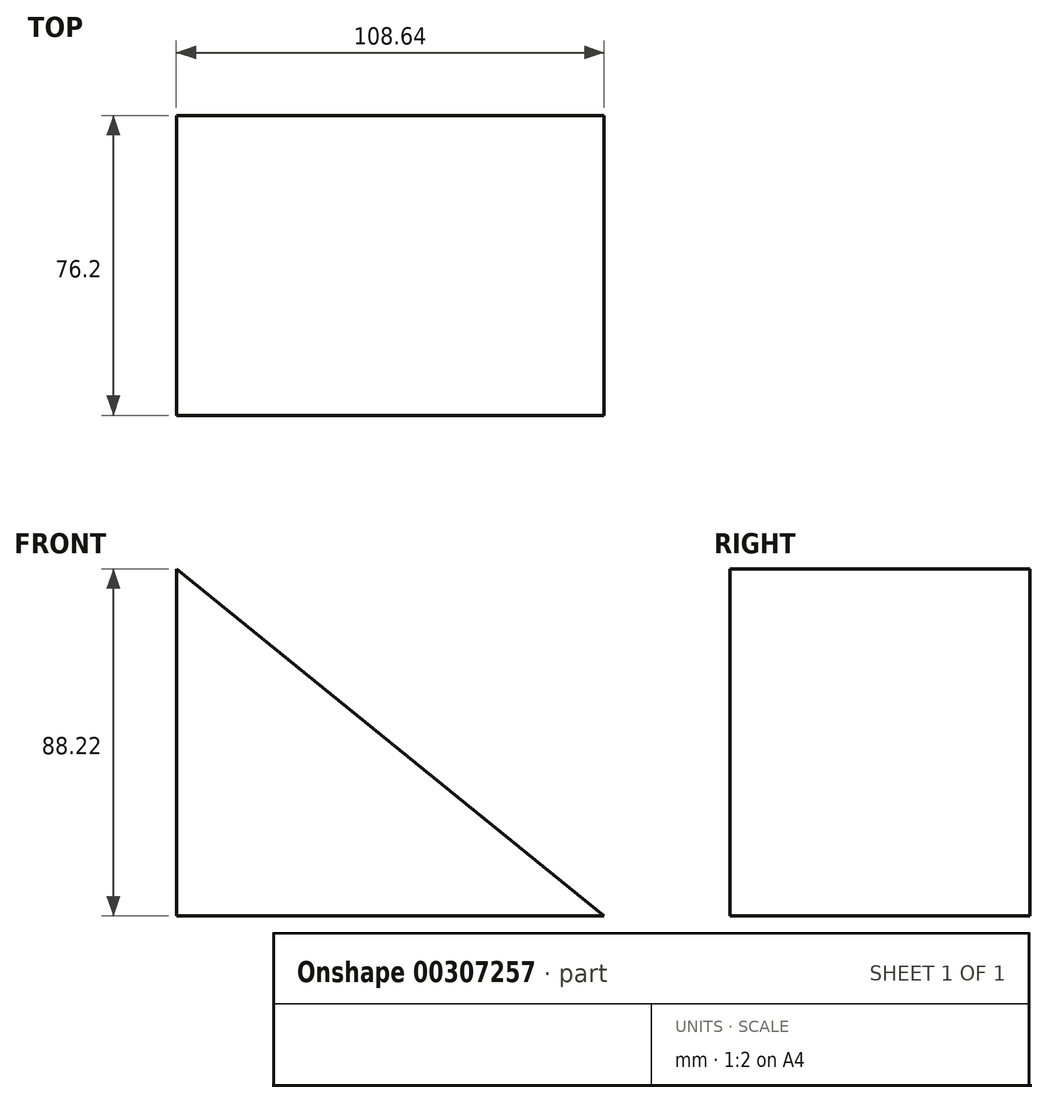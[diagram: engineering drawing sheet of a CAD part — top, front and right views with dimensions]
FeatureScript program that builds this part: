
annotation { "Feature Type Name" : "Feature", "Feature Type Description" : "" }
export const myFeature = defineFeature(function(context is Context, id is Id, definition is map)
    precondition{}
    {
        {
            var Q0;
            Q0=qCreatedBy(makeId("Front.planeOp"),FACE);
            var sketch = newSketch(context, id + "F0", { "sketchPlane" : qUnion([Q0])});
            skLineSegment(sketch, "E0", {"start": v(-51.69, -43.49) * mm, "end": v(56.95, -43.49) * mm});
            skLineSegment(sketch, "E1", {"start": v(56.95, -43.49) * mm, "end": v(-51.69, 44.73) * mm});
            skLineSegment(sketch, "E2", {"start": v(-51.69, 44.73) * mm, "end": v(-51.69, -43.49) * mm});
            skSolve(sketch);
        }
        {
            var Q0;
            Q0=makeQuery(id+"F0.imprint","IMPRINT",FACE,{"disambiguationData":[TD([[makeQuery(id+"F0.imprint","IMPRINT",EDGE,{"derivedFrom":sQuery(id+"F0.wireOp",EDGE,"E0")}),1.0]])]});
            extrude(context, id + "F1", {"entities" : qUnion([Q0]), "depth" : 76.2 * mm});
        }
    });
